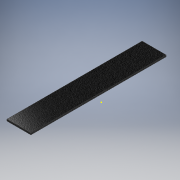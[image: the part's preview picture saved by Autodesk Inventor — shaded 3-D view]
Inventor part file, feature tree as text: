
AUTODESK INVENTOR PART (.ipt)
format: ipt  version: 2018 (Build 220112000, 112)  size: 98,816 bytes
history: native  units: in
note: dims shown in document units (in); Inventor stores cm internally (conversion verified against a paired STEP export)
features: sketch x2, extrude x1
ambient origin geometry x8: Origin, YZ Plane, XZ Plane, XY Plane, X Axis, Y Axis, Z Axis, Center Point
bodies: Solid1 (feature_tree)
feature tree (3):
  sketch  "Sketch1"  dims[d0=6.2205in d1=1.1024in]
  extrude  "Extrusion1"  Depth=1.1024in
  sketch  "Sketch2"  dims[d2=0.0787in d3=0.0in]
